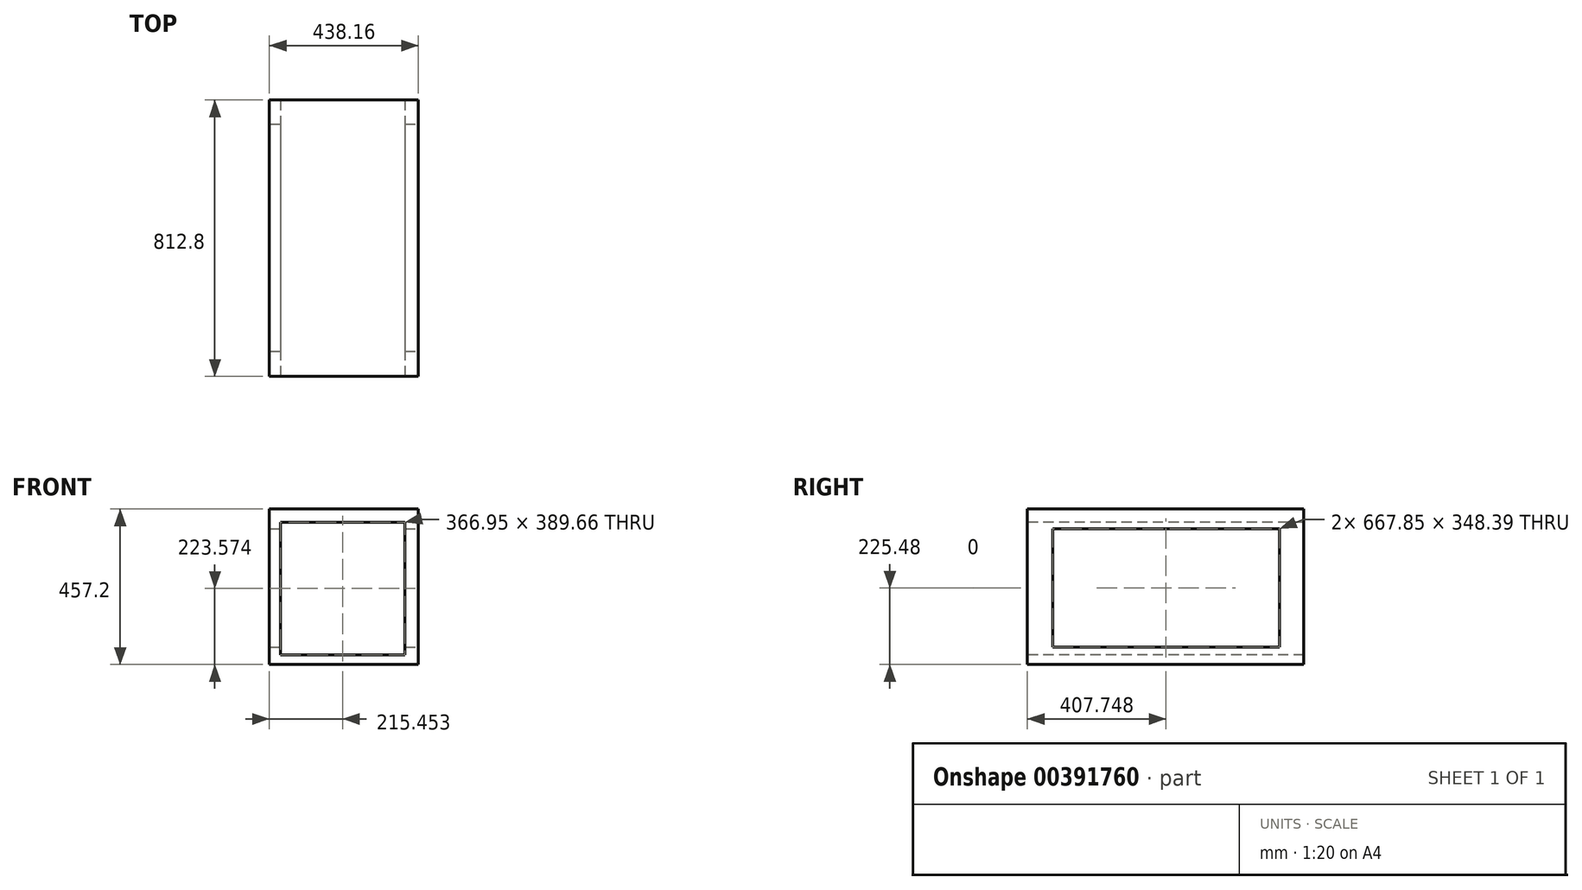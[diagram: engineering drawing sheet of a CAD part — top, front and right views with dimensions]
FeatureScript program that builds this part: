
annotation { "Feature Type Name" : "Feature", "Feature Type Description" : "" }
export const myFeature = defineFeature(function(context is Context, id is Id, definition is map)
    precondition{}
    {
        {
            var Q0;
            Q0=qCreatedBy(makeId("Front.planeOp"),FACE);
            var sketch = newSketch(context, id + "F0", { "sketchPlane" : qUnion([Q0])});
            skLineSegment(sketch, "E0.bottom", {"start": v(219.08, -228.6) * mm, "end": v(-219.08, -228.6) * mm});
            skLineSegment(sketch, "E0.top", {"start": v(219.08, 228.6) * mm, "end": v(-219.07, 228.6) * mm});
            skLineSegment(sketch, "E0.left", {"start": v(219.08, -228.6) * mm, "end": v(219.08, 228.6) * mm});
            skLineSegment(sketch, "E0.right", {"start": v(-219.08, -228.6) * mm, "end": v(-219.07, 228.6) * mm});
            skPoint(sketch, "E0.middle", {"position": v(0, 0) * mm});
            skSolve(sketch);
        }
        {
            var Q0;
            Q0=makeQuery(id+"F0.imprint","IMPRINT",FACE,{"disambiguationData":[TD([[makeQuery(id+"F0.imprint","IMPRINT",EDGE,{"derivedFrom":sQuery(id+"F0.wireOp",EDGE,"E0.bottom")}),-1.0]])]});
            extrude(context, id + "F1", {"entities" : qUnion([Q0]), "oppositeDirection" : true, "depth" : 812.8 * mm});
        }
        {
            var Q0;
            Q0=makeQuery(id+"F1.opExtrude","CAP_FACE",FACE,{"disambiguationData":[OSD([sQuery(id+"F0.wireOp",EDGE,"E0.bottom"),sQuery(id+"F0.wireOp",EDGE,"E0.top"),sQuery(id+"F0.wireOp",EDGE,"E0.left"),sQuery(id+"F0.wireOp",EDGE,"E0.right")])],"isStart":true});
            var sketch = newSketch(context, id + "F2", { "sketchPlane" : qUnion([Q0])});
            skText(sketch, "E1", { "text": "TIG", "fontName": "OpenSans-Regular.ttf"});
            const initialGuessF2  = {"E1": [-0.0627, -0.0366, 1, 0, 0.06072]};
            skSetInitialGuess(sketch, initialGuessF2);
            skSolve(sketch);
        }
        {
            var Q0;
            Q0=qSketchRegion(id+"F2",true);
            extrude(context, id + "F3", {"entities" : qUnion([Q0]), "operationType" : NewBodyOperationType.REMOVE, "oppositeDirection" : true, "depth" : 25.4 * mm});
        }
        {
            var Q0;
            Q0=makeQuery(id+"F1.opExtrude","CAP_FACE",FACE,{"disambiguationData":[OSD([sQuery(id+"F0.wireOp",EDGE,"E0.bottom"),sQuery(id+"F0.wireOp",EDGE,"E0.top"),sQuery(id+"F0.wireOp",EDGE,"E0.left"),sQuery(id+"F0.wireOp",EDGE,"E0.right")])],"isStart":true});
            var sketch = newSketch(context, id + "F4", { "sketchPlane" : qUnion([Q0])});
            skLineSegment(sketch, "E2.bottom", {"start": v(-187.1, 189.8) * mm, "end": v(179.85, 189.8) * mm});
            skLineSegment(sketch, "E2.top", {"start": v(-187.1, -199.85) * mm, "end": v(179.85, -199.85) * mm});
            skLineSegment(sketch, "E2.left", {"start": v(-187.1, 189.8) * mm, "end": v(-187.1, -199.85) * mm});
            skLineSegment(sketch, "E2.right", {"start": v(179.85, 189.8) * mm, "end": v(179.85, -199.85) * mm});
            skSolve(sketch);
        }
        {
            var Q0;
            Q0 = qSketchRegion(id + "F4", true);
            extrude(context, id + "F5", {"entities" : qUnion([Q0]), "operationType" : NewBodyOperationType.REMOVE, "endBound" : BoundingType.THROUGH_ALL, "oppositeDirection" : true, "depth" : 381 * mm});
        }
        {
            var Q0;
            Q0=makeQuery(id+"F1.opExtrude","SWEPT_FACE",FACE,{"disambiguationData":[OSD([sQuery(id+"F0.wireOp",EDGE,"E0.left")])]});
            var sketch = newSketch(context, id + "F6", { "sketchPlane" : qUnion([Q0])});
            skLineSegment(sketch, "E3.bottom", {"start": v(73.82, 171.08) * mm, "end": v(741.67, 171.08) * mm});
            skLineSegment(sketch, "E3.top", {"start": v(73.82, -177.32) * mm, "end": v(741.67, -177.32) * mm});
            skLineSegment(sketch, "E3.left", {"start": v(73.82, 171.08) * mm, "end": v(73.82, -177.32) * mm});
            skLineSegment(sketch, "E3.right", {"start": v(741.67, 171.08) * mm, "end": v(741.67, -177.32) * mm});
            skSolve(sketch);
        }
        {
            var Q0;
            Q0 = qSketchRegion(id + "F6", true);
            extrude(context, id + "F7", {"entities" : qUnion([Q0]), "operationType" : NewBodyOperationType.REMOVE, "endBound" : BoundingType.THROUGH_ALL, "oppositeDirection" : true, "depth" : 25.4 * mm});
        }
    });
